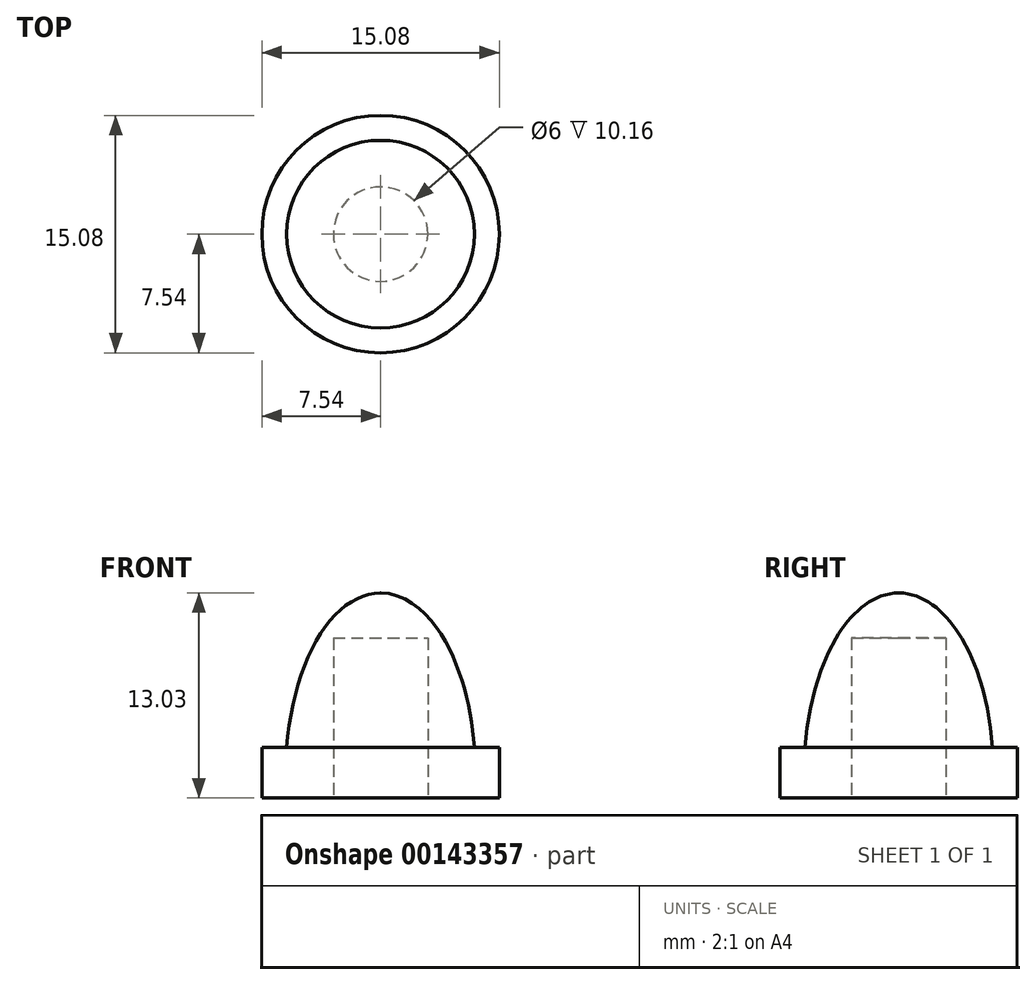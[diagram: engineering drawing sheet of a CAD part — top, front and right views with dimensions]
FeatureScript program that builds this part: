
annotation { "Feature Type Name" : "Feature", "Feature Type Description" : "" }
export const myFeature = defineFeature(function(context is Context, id is Id, definition is map)
    precondition{}
    {
        {
            var Q0;
            Q0=qCreatedBy(makeId("Front.planeOp"),FACE);
            var sketch = newSketch(context, id + "F0", { "sketchPlane" : qUnion([Q0])});
            skPoint(sketch, "E0.middle", {"position": v(0, 0) * mm});
            skLineSegment(sketch, "E1", {"start": v(-5.96, 0) * mm, "end": v(-4.38, 0) * mm});
            skPoint(sketch, "E2.orphan", {"position": v(-11.43, -11.96) * mm});
            skPoint(sketch, "E3.orphan", {"position": v(11.43, -11.96) * mm});
            skPoint(sketch, "E0.left.start.orphan", {"position": v(-11.43, 11.96) * mm});
            skPoint(sketch, "E0.right.start.orphan", {"position": v(11.43, 11.96) * mm});
            skLineSegment(sketch, "E4.bottom", {"start": v(-7.54, 0) * mm, "end": v(-4.38, 0) * mm});
            skLineSegment(sketch, "E4.top", {"start": v(-7.54, -3.23) * mm, "end": v(0, -3.23) * mm});
            skLineSegment(sketch, "E4.left", {"start": v(-7.54, 0) * mm, "end": v(-7.54, -3.23) * mm});
            skPoint(sketch, "E4.middle", {"position": v(0, -1.62) * mm});
            skLineSegment(sketch, "E5", {"start": v(0, 16.36) * mm, "end": v(0, -3.23) * mm});
            skPoint(sketch, "E4.right.end.orphan", {"position": v(7.54, -3.23) * mm});
            skPoint(sketch, "E6.trimOffspring.end.orphan", {"position": v(7.54, 0) * mm});
            skEllipse(sketch, "E7", {"center": v(0, -1.62) * mm, "majorRadius": 11.41 * mm, "minorRadius": 6.02 * mm, "majorAxis": v(0, 1)});
            skSolve(sketch);
        }
        {
            var Q0;
            {var subQ3=sQuery(id+"F0.wireOp",EDGE,"cb71bb47-9fbb-4b35-a6fa-61e1c4ad62da.trimOffspring");Q0=makeQuery(id+"F0.imprint","IMPRINT",FACE,{"disambiguationData":[TD([[makeQuery(id+"F0.imprint","IMPRINT",EDGE,{"derivedFrom":subQ3}),1.0]])]});}
            var Q1;
            {var subQ1=sQuery(id+"F0.wireOp",EDGE,"E4.top");Q1=makeQuery(id+"F0.imprint","IMPRINT",FACE,{"disambiguationData":[TD([[makeQuery(id+"F0.imprint","IMPRINT",EDGE,{"derivedFrom":subQ1}),1.0]])]});}
            var Q2;
            Q2=sQuery(id+"F0.wireOp",EDGE,"E5");
            revolve(context, id + "F1", {"entities" : qUnion([Q0, Q1]), "axis" : qUnion([Q2]), "revolveType" : RevolveType.FULL});
        }
        {
            var Q0;
            Q0=makeQuery(id+"F1.opRevolve","SWEPT_FACE",FACE,{"disambiguationData":[OSD([sQuery(id+"F0.wireOp",EDGE,"E4.top")])]});
            var sketch = newSketch(context, id + "F2", { "sketchPlane" : qUnion([Q0])});
            skCircle(sketch, "E8", {"center": v(0, 0) * mm, "radius": 3 * mm});
            skSolve(sketch);
        }
        {
            var Q0;
            Q0=makeQuery(id+"F2.imprint","IMPRINT",FACE,{"disambiguationData":[TD([[makeQuery(id+"F2.imprint","IMPRINT",EDGE,{"derivedFrom":sQuery(id+"F2.wireOp",EDGE,"E8")}),1.0]])]});
            extrude(context, id + "F3", {"entities" : qUnion([Q0]), "operationType" : NewBodyOperationType.REMOVE, "oppositeDirection" : true, "depth" : 10.16 * mm});
        }
    });
